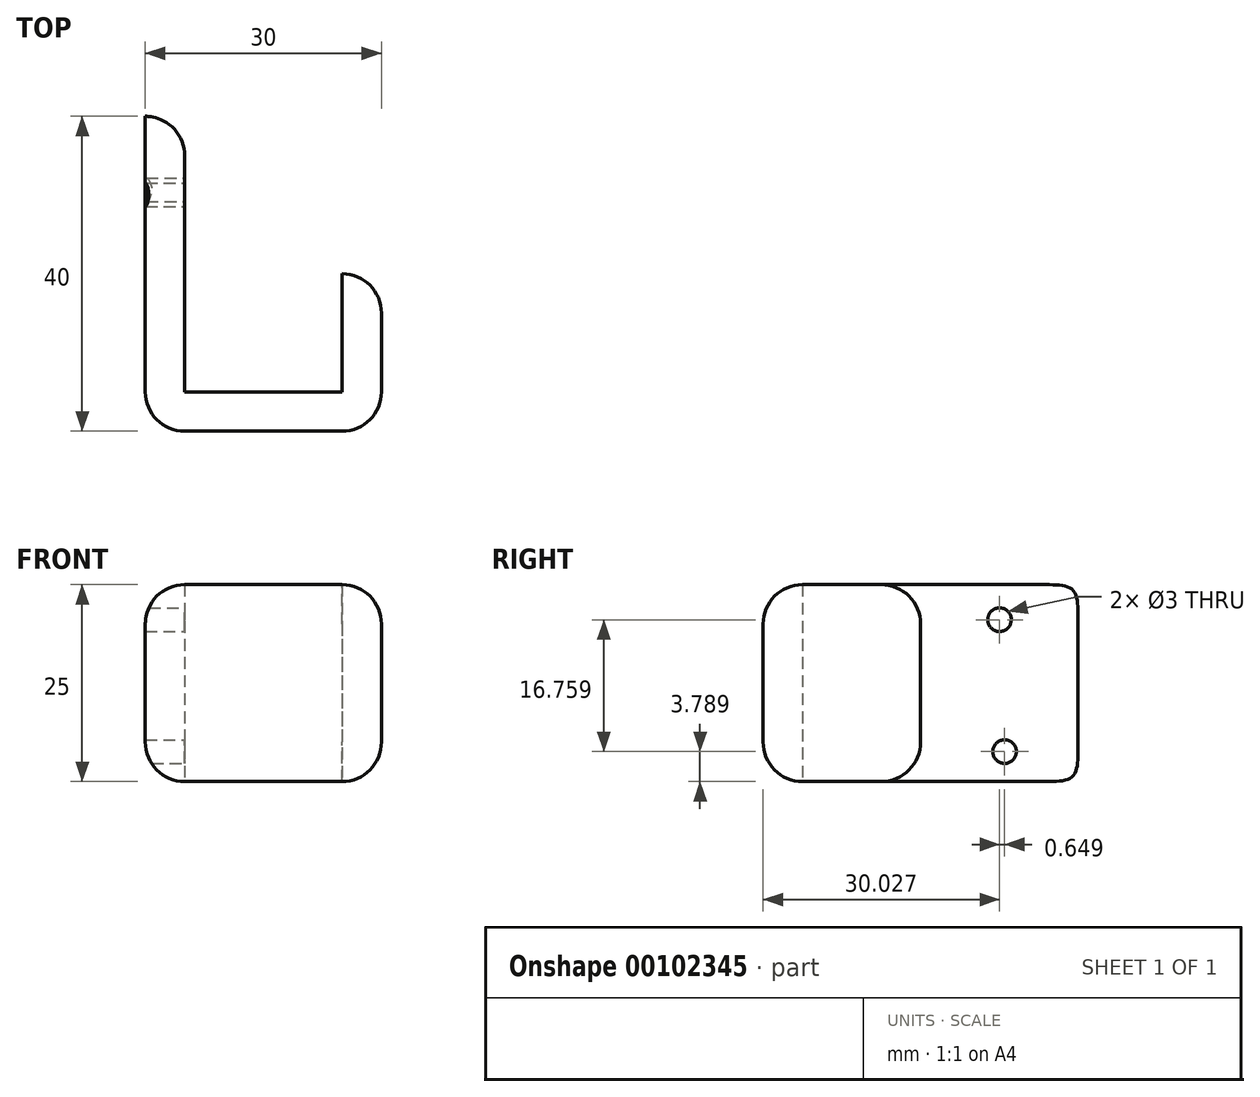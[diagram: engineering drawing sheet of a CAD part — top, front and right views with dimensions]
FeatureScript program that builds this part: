
annotation { "Feature Type Name" : "Feature", "Feature Type Description" : "" }
export const myFeature = defineFeature(function(context is Context, id is Id, definition is map)
    precondition{}
    {
        {
            var Q0;
            Q0=qCreatedBy(makeId("Top.planeOp"),FACE);
            var sketch = newSketch(context, id + "F0", { "sketchPlane" : qUnion([Q0])});
            skLineSegment(sketch, "E0", {"start": v(-60.52, 43.44) * mm, "end": v(-60.52, 3.44) * mm});
            skLineSegment(sketch, "E1", {"start": v(-60.52, 3.44) * mm, "end": v(-30.52, 3.44) * mm});
            skLineSegment(sketch, "E2", {"start": v(-30.52, 3.44) * mm, "end": v(-30.52, 23.44) * mm});
            skLineSegment(sketch, "E3", {"start": v(-30.52, 23.44) * mm, "end": v(-35.52, 23.44) * mm});
            skLineSegment(sketch, "E4", {"start": v(-35.52, 23.44) * mm, "end": v(-35.52, 8.44) * mm});
            skLineSegment(sketch, "E5", {"start": v(-35.52, 8.44) * mm, "end": v(-55.52, 8.44) * mm});
            skLineSegment(sketch, "E6", {"start": v(-55.52, 8.44) * mm, "end": v(-55.52, 43.44) * mm});
            skLineSegment(sketch, "E7", {"start": v(-55.52, 43.44) * mm, "end": v(-60.52, 43.44) * mm});
            skSolve(sketch);
        }
        {
            var Q0;
            Q0 = qSketchRegion(id + "F0", true);
            extrude(context, id + "F1", {"entities" : qUnion([Q0]), "depth" : 25 * mm});
        }
        {
            var Q0;
            Q0=makeQuery(id+"F1.opExtrude","CAP_EDGE",EDGE,{"disambiguationData":[OSD([sQuery(id+"F0.wireOp",EDGE,"E1")])],"isStart":false});
            fillet(context, id + "F2", {"entities" : qUnion([Q0]), "radius" : 5 * mm, "tangentPropagation" : true, "allowEdgeOverflow" : false});
        }
        {
            var Q0;
            Q0=makeQuery(id+"F1.opExtrude","CAP_EDGE",EDGE,{"disambiguationData":[OSD([sQuery(id+"F0.wireOp",EDGE,"E2")])],"isStart":false});
            fillet(context, id + "F3", {"entities" : qUnion([Q0]), "radius" : 5 * mm, "tangentPropagation" : true, "allowEdgeOverflow" : false});
        }
        {
            var Q0;
            Q0=makeQuery(id+"F1.opExtrude","CAP_EDGE",EDGE,{"disambiguationData":[OSD([sQuery(id+"F0.wireOp",EDGE,"E2")])],"isStart":true});
            fillet(context, id + "F4", {"entities" : qUnion([Q0]), "radius" : 5 * mm, "tangentPropagation" : true, "allowEdgeOverflow" : false});
        }
        {
            var Q0;
            Q0=makeQuery(id+"F1.opExtrude","CAP_EDGE",EDGE,{"disambiguationData":[OSD([sQuery(id+"F0.wireOp",EDGE,"E0")])],"isStart":false});
            fillet(context, id + "F5", {"entities" : qUnion([Q0]), "radius" : 5 * mm, "tangentPropagation" : true, "allowEdgeOverflow" : false});
        }
        {
            var Q0;
            Q0=makeQuery(id+"F1.opExtrude","SWEPT_EDGE",EDGE,{"disambiguationData":[OSD([sQuery(id+"F0.wireOp",EDGE,"E6"),sQuery(id+"F0.wireOp",EDGE,"E7")])]});
            fillet(context, id + "F6", {"entities" : qUnion([Q0]), "radius" : 5 * mm, "tangentPropagation" : true, "allowEdgeOverflow" : false});
        }
        {
            var Q0;
            Q0=makeQuery(id+"F1.opExtrude","SWEPT_EDGE",EDGE,{"disambiguationData":[OSD([sQuery(id+"F0.wireOp",EDGE,"E2"),sQuery(id+"F0.wireOp",EDGE,"E3")])]});
            fillet(context, id + "F7", {"entities" : qUnion([Q0]), "radius" : 5 * mm, "tangentPropagation" : true, "allowEdgeOverflow" : false});
        }
        {
            var Q0;
            Q0=qCreatedBy(makeId("Right.planeOp"),FACE);
            cPlane(context, id + "F8", {"entities" : qUnion([Q0]), "cplaneType" : CPlaneType.OFFSET, "offset" : 55 * mm, "oppositeDirection" : true, "width" : 150 * mm, "height" : 150 * mm});
        }
        {
            var Q0;
            Q0=qCreatedBy(id+"F8.planeOp",FACE);
            var sketch = newSketch(context, id + "F9", { "sketchPlane" : qUnion([Q0])});
            skCircle(sketch, "E8", {"center": v(33.47, 20.55) * mm, "radius": 1.5 * mm});
            skCircle(sketch, "E9", {"center": v(34.12, 3.79) * mm, "radius": 1.5 * mm});
            skSolve(sketch);
        }
        {
            var Q0;
            Q0=makeQuery(id+"F9.imprint","IMPRINT",FACE,{"disambiguationData":[TD([[makeQuery(id+"F9.imprint","IMPRINT",EDGE,{"derivedFrom":sQuery(id+"F9.wireOp",EDGE,"E8")}),1.0]])]});
            extrude(context, id + "F10", {"entities" : qUnion([Q0]), "operationType" : NewBodyOperationType.REMOVE, "oppositeDirection" : true, "depth" : 6 * mm});
        }
        {
            var Q0;
            Q0 = qSketchRegion(id + "F9", true);
            extrude(context, id + "F11", {"entities" : qUnion([Q0]), "operationType" : NewBodyOperationType.REMOVE, "oppositeDirection" : true, "depth" : 6 * mm});
        }
    });
